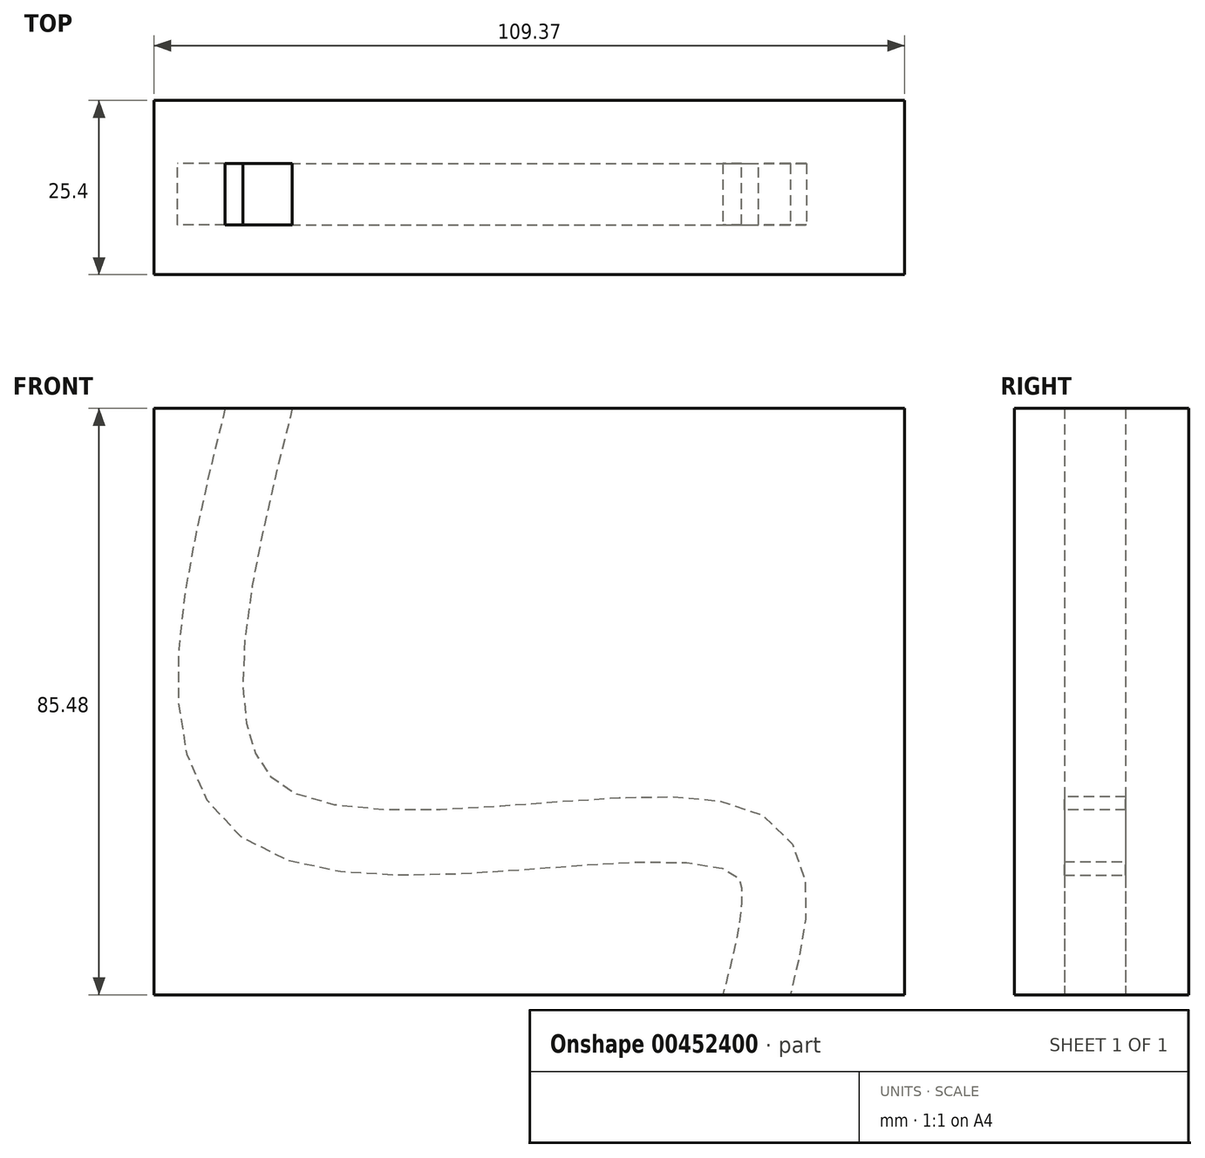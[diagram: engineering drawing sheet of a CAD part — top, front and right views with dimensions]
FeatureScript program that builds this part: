
annotation { "Feature Type Name" : "Feature", "Feature Type Description" : "" }
export const myFeature = defineFeature(function(context is Context, id is Id, definition is map)
    precondition{}
    {
        {
            var Q0;
            Q0=qCreatedBy(makeId("Front.planeOp"),FACE);
            var sketch = newSketch(context, id + "F0", { "sketchPlane" : qUnion([Q0])});
            skLineSegment(sketch, "E0.bottom", {"start": v(-44.9, 42.88) * mm, "end": v(64.47, 42.88) * mm});
            skLineSegment(sketch, "E0.top", {"start": v(-44.9, -42.6) * mm, "end": v(64.47, -42.6) * mm});
            skLineSegment(sketch, "E0.left", {"start": v(-44.9, 42.88) * mm, "end": v(-44.9, -42.6) * mm});
            skLineSegment(sketch, "E0.right", {"start": v(64.47, 42.88) * mm, "end": v(64.47, -42.6) * mm});
            skSolve(sketch);
        }
        {
            var Q0;
            Q0=makeQuery(id+"F0.imprint","IMPRINT",FACE,{"disambiguationData":[TD([[makeQuery(id+"F0.imprint","IMPRINT",EDGE,{"derivedFrom":sQuery(id+"F0.wireOp",EDGE,"E0.bottom")}),-1.0]])]});
            extrude(context, id + "F1", {"entities" : qUnion([Q0]), "depth" : 25.4 * mm});
        }
        {
            var Q0;
            Q0=makeQuery(id+"F1.opExtrude","SWEPT_FACE",FACE,{"disambiguationData":[OSD([sQuery(id+"F0.wireOp",EDGE,"E0.bottom")])]});
            var sketch = newSketch(context, id + "F2", { "sketchPlane" : qUnion([Q0])});
            skLineSegment(sketch, "E1.bottom", {"start": v(-34.54, -9.2) * mm, "end": v(-24.75, -9.2) * mm});
            skLineSegment(sketch, "E1.top", {"start": v(-34.54, -18.13) * mm, "end": v(-24.75, -18.13) * mm});
            skLineSegment(sketch, "E1.left", {"start": v(-34.54, -9.2) * mm, "end": v(-34.54, -18.13) * mm});
            skLineSegment(sketch, "E1.right", {"start": v(-24.75, -9.2) * mm, "end": v(-24.75, -18.13) * mm});
            skSolve(sketch);
        }
        {
            var Q0;
            Q0=makeQuery(id+"F1.opExtrude","CAP_FACE",FACE,{"disambiguationData":[OSD([sQuery(id+"F0.wireOp",EDGE,"E0.bottom"),sQuery(id+"F0.wireOp",EDGE,"E0.top"),sQuery(id+"F0.wireOp",EDGE,"E0.left"),sQuery(id+"F0.wireOp",EDGE,"E0.right")])],"isStart":true});
            var sketch = newSketch(context, id + "F3", { "sketchPlane" : qUnion([Q0])});
            skFitSpline(sketch, "E2", {"points": [v(29.36, 42.88) * mm, v(27.34, -16.7) * mm, v(-41.16, -20.15) * mm, v(-43.17, -42.6) * mm], "startDerivative": vector(51.88, -207.4) * mm, "endDerivative": vector(32.05, -123.66) * mm});
            skSolve(sketch);
        }
        {
            var Q0;
            Q0=makeQuery(id+"F2.imprint","IMPRINT",FACE,{"disambiguationData":[TD([[makeQuery(id+"F2.imprint","IMPRINT",EDGE,{"derivedFrom":sQuery(id+"F2.wireOp",EDGE,"E1.bottom")}),-1.0]])]});
            var Q1;
            Q1=sQuery(id+"F3.wireOp",EDGE,"E2");
            sweep(context, id + "F4", {"operationType" : NewBodyOperationType.REMOVE, "profiles" : qUnion([Q0]), "path" : qUnion([Q1])});
        }
    });
